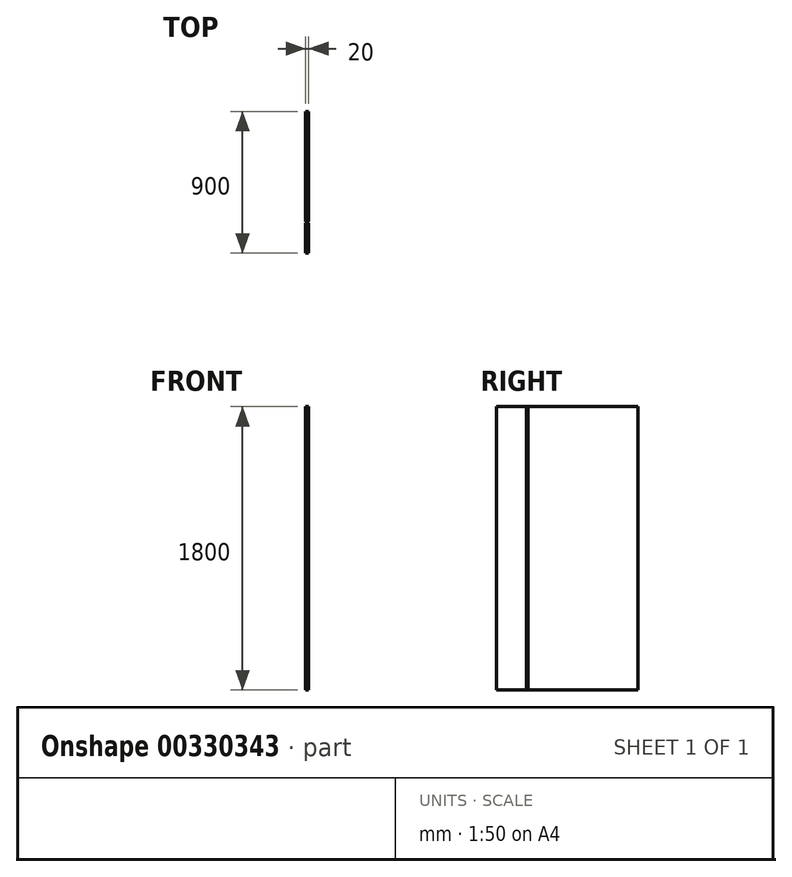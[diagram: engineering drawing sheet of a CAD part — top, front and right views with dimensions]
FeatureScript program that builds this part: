
annotation { "Feature Type Name" : "Feature", "Feature Type Description" : "" }
export const myFeature = defineFeature(function(context is Context, id is Id, definition is map)
    precondition{}
    {
        {
            var Q0;
            Q0=qCreatedBy(makeId("Top.planeOp"),FACE);
            var sketch = newSketch(context, id + "F0", { "sketchPlane" : qUnion([Q0])});
            skLineSegment(sketch, "E0.bottom", {"start": v(0, 0) * mm, "end": v(20, 0) * mm});
            skLineSegment(sketch, "E0.top", {"start": v(0, -700) * mm, "end": v(20, -700) * mm});
            skLineSegment(sketch, "E0.left", {"start": v(0, 0) * mm, "end": v(0, -700) * mm});
            skLineSegment(sketch, "E0.right", {"start": v(20, 0) * mm, "end": v(20, -700) * mm});
            skLineSegment(sketch, "E1.bottom", {"start": v(20, -710) * mm, "end": v(0, -710) * mm});
            skLineSegment(sketch, "E1.top", {"start": v(20, -900) * mm, "end": v(0, -900) * mm});
            skLineSegment(sketch, "E1.left", {"start": v(20, -710) * mm, "end": v(20, -900) * mm});
            skLineSegment(sketch, "E1.right", {"start": v(0, -710) * mm, "end": v(0, -900) * mm});
            skLineSegment(sketch, "E2.bottom", {"start": v(6.81, -700) * mm, "end": v(13.42, -700) * mm});
            skLineSegment(sketch, "E2.top", {"start": v(6.81, -710) * mm, "end": v(13.42, -710) * mm});
            skLineSegment(sketch, "E2.left", {"start": v(6.81, -700) * mm, "end": v(6.81, -710) * mm});
            skLineSegment(sketch, "E2.right", {"start": v(13.42, -700) * mm, "end": v(13.42, -710) * mm});
            skSolve(sketch);
        }
        {
            var Q0;
            Q0=qSketchRegion(id+"F0",true);
            extrude(context, id + "F1", {"entities" : qUnion([Q0]), "offsetDistance" : 25 * mm, "depth" : 1800 * mm});
        }
    });
